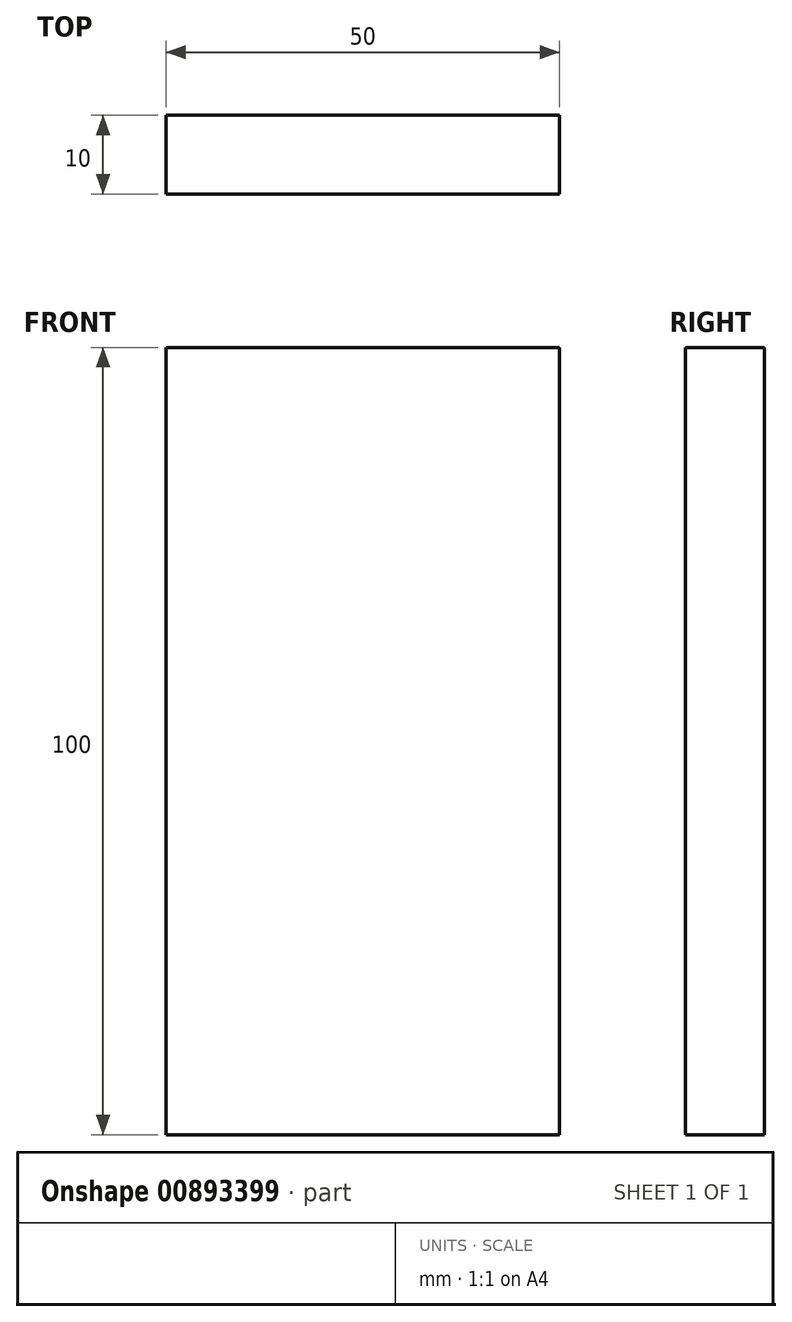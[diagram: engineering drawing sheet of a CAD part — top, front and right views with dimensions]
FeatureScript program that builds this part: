
annotation { "Feature Type Name" : "Feature", "Feature Type Description" : "" }
export const myFeature = defineFeature(function(context is Context, id is Id, definition is map)
    precondition{}
    {
        {
            var Q0;
            Q0=qCreatedBy(makeId("Front.planeOp"),FACE);
            var sketch = newSketch(context, id + "F0", { "sketchPlane" : qUnion([Q0])});
            skLineSegment(sketch, "E0.bottom", {"start": v(0, 0) * mm, "end": v(50, 0) * mm});
            skLineSegment(sketch, "E0.top", {"start": v(0, 100) * mm, "end": v(50, 100) * mm});
            skLineSegment(sketch, "E0.left", {"start": v(0, 0) * mm, "end": v(0, 100) * mm});
            skLineSegment(sketch, "E0.right", {"start": v(50, 0) * mm, "end": v(50, 100) * mm});
            skSolve(sketch);
        }
        {
            var Q0;
            Q0 = qSketchRegion(id + "F0", true);
            extrude(context, id + "F1", {"entities" : qUnion([Q0]), "depth" : 10 * mm, "offsetDistance" : 25 * mm});
        }
    });
